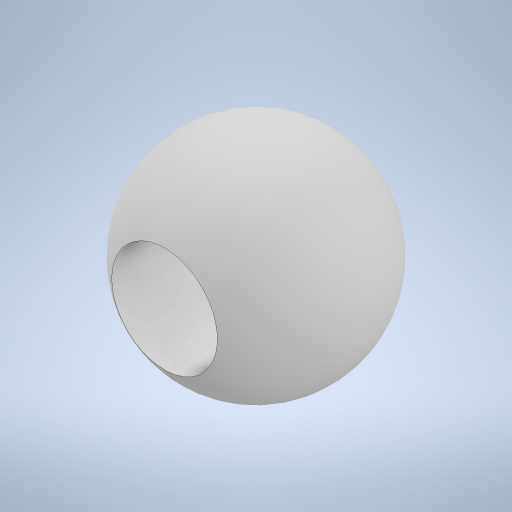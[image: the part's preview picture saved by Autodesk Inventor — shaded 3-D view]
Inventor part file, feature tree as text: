
AUTODESK INVENTOR PART (.ipt)
format: ipt  version: 2024 (Build 280153000, 153)  size: 248,832 bytes
history: native  units: in
note: dims shown in document units (in); Inventor stores cm internally (conversion verified against a paired STEP export)
features: sketch x1, revolve x1, extrude x1, direct_edit x1, other x1
ambient origin geometry x8: Origin, YZ Plane, XZ Plane, XY Plane, X Axis, Y Axis, Z Axis, Center Point
bodies: Solid1 (feature_tree)
feature tree (5):
  sketch  "Sketch1"  dims[d0=0.125in d1=0.125in d2=90.0deg d3=0.25in d4=0.0in d5=3.937in d6=0.3937in d7=0.3937in]
  revolve  "Revolution1"  [1 undecoded]
  extrude  "Extrusion1"  TaperAngle=90.0deg  [1 undecoded]
  direct_edit  "Direct Edit1"
  other  "Scale1"
note: 2 required parameter values undecoded (feature->parameter linkage not recoverable at this tier; creation-order binding heuristic only, values carry confidence <= 0.55)